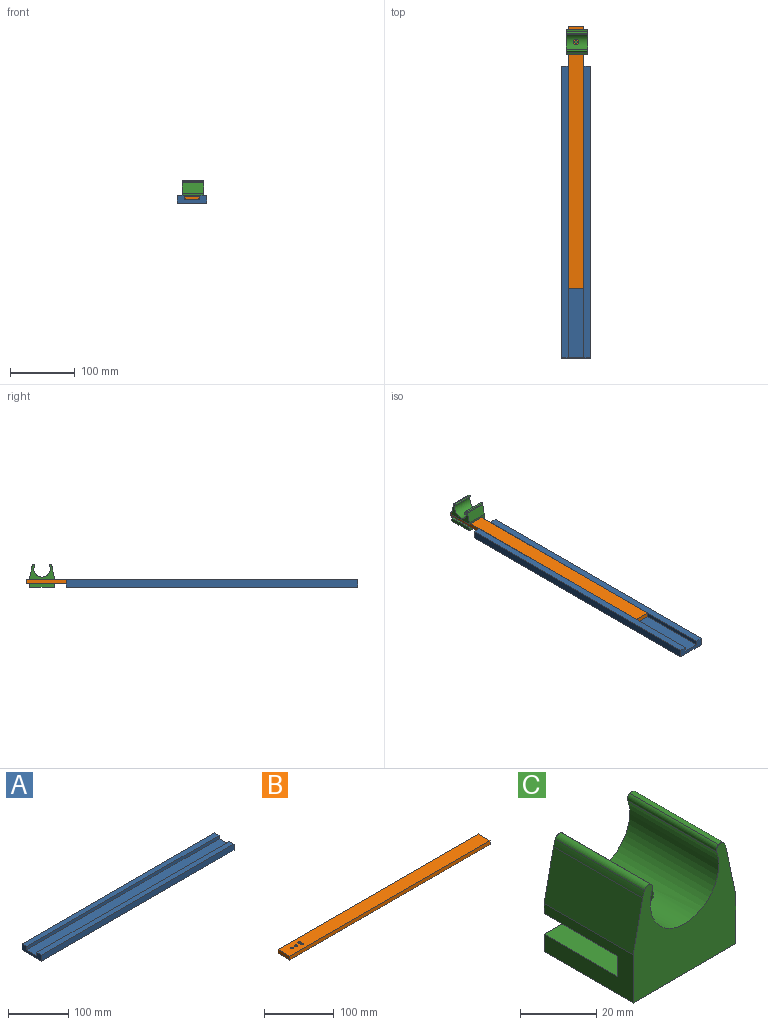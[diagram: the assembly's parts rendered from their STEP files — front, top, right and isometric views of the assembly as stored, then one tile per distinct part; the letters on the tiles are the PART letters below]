
ASSEMBLY  parts=3 mates=2
PART A: 10 faces, bbox 450.9x45.7x12.2 mm
  f0: plane 450.85x6.6mm, normal (0,1,0), area 2977.4mm2, adj f1,f7,f8,f9
  f1: plane 450.85x10.8mm, normal (0,0,1), area 4866.9mm2, adj f0,f2,f8,f9
  f2: plane 450.85x12.19mm, normal (0,-1,0), area 5496.8mm2, adj f1,f3,f8,f9
  f3: plane 450.85x45.72mm, normal (0,0,-1), area 20612.9mm2, adj f2,f4,f8,f9
  f4: plane 450.85x12.19mm, normal (0,1,0), area 5496.8mm2, adj f3,f5,f8,f9
  f5: plane 450.85x10.8mm, normal (0,0,1), area 4866.9mm2, adj f4,f6,f8,f9
  f6: plane 450.85x6.6mm, normal (0,-1,0), area 2977.4mm2, adj f5,f7,f8,f9
  f7: plane 450.85x24.13mm, normal (0,0,1), area 10879mm2, adj f0,f6,f8,f9
  f8: plane 45.72x12.19mm, normal (1,0,0), area 398.1mm2, adj f0,f1,f2,f3,f4,f5,f6,f7
  f9: plane 45.72x12.19mm, normal (-1,0,0), area 398.1mm2, adj f0,f1,f2,f3,f4,f5,f6,f7
PART B: 17 faces, bbox 406.4x24.1x6.6 mm
  f0: plane 406.4x24.13mm, normal (0,0,-1), area 1690.2mm2, adj f7,f9,f10,f11,f12,f13,f14,f15
  f1: cylinder r=2.03mm len=4.06mm, axis (0,0,1), area 25.9mm2, adj f8,f16
  f2: cylinder r=2.16mm len=4.32mm, axis (0,0,1), area 27.6mm2, adj f8,f16
  f3: cylinder r=2.16mm len=4.32mm, axis (0,0,1), area 13.8mm2, adj f4,f6,f8,f16
  f4: plane 4.83x2.03mm, normal (1,0,0), area 9.8mm2, adj f3,f5,f8,f16
  f5: cylinder r=2.16mm len=4.32mm, axis (0,0,1), area 13.8mm2, adj f4,f6,f8,f16
  f6: plane 4.83x2.03mm, normal (-1,0,0), area 9.8mm2, adj f3,f5,f8,f16
  f7: plane 406.4x6.6mm, normal (0,1,0), area 2683.9mm2, adj f0,f8,f10,f11
  f8: plane 406.4x24.13mm, normal (0,0,1), area 9743.3mm2, adj f1,f2,f3,f4,f5,f6,f7,f9
  f9: plane 406.4x6.6mm, normal (0,-1,0), area 2683.9mm2, adj f0,f8,f10,f11
  f10: plane 24.13x6.6mm, normal (1,0,0), area 159.4mm2, adj f0,f7,f8,f9
  f11: plane 24.13x6.6mm, normal (-1,0,0), area 159.4mm2, adj f0,f7,f8,f9
  f12: plane 402.44x4.57mm, normal (0,-1,0), area 1839.9mm2, adj f0,f13,f15,f16
  f13: plane 20.17x4.57mm, normal (-1,0,0), area 92.2mm2, adj f0,f12,f14,f16
  f14: plane 402.44x4.57mm, normal (0,1,0), area 1839.9mm2, adj f0,f13,f15,f16
  f15: plane 20.17x4.57mm, normal (1,0,0), area 92.2mm2, adj f0,f12,f14,f16
  f16: plane 402.44x20.17mm, normal (0,0,-1), area 8053.1mm2, adj f1,f2,f3,f4,f5,f6,f12,f13
PART C: 19 faces, bbox 38.1x33x35.1 mm
  f0: plane 38.1x27.31mm, normal (0,0,1), area 1040.3mm2, adj f1,f5,f6,f7
  f1: plane 38.1x6.6mm, normal (0,1,0), area 251.6mm2, adj f0,f2,f6,f7
  f2: plane 38.1x27.31mm, normal (0,0,-1), area 978.2mm2, adj f1,f3,f6,f7,f17
  f3: plane 38.1x22.91mm, normal (0,1,0), area 374.4mm2, adj f2,f6,f7,f8,f9,f10,f11,f12
  f4: plane 38.1x33.02mm, normal (0,0,-1), area 1258.1mm2, adj f5,f6,f7,f18
  f5: plane 38.1x5.59mm, normal (0,1,0), area 212.9mm2, adj f0,f4,f6,f7
  f6: plane 33.02x15.37mm, normal (1,0,0), area 327.1mm2, adj f0,f1,f2,f3,f4,f5,f10,f18
  f7: plane 33.02x15.37mm, normal (-1,0,0), area 327.1mm2, adj f0,f1,f2,f3,f4,f5,f9,f18
  f8: cylinder r=15.88mm len=33.02mm, axis (0,-1,0), area 74.7mm2, adj f3,f9,f14,f18
  f9: plane 33.02x16.52mm, normal (-0.98,0,0.21), area 557.8mm2, adj f3,f7,f8,f18
  f10: plane 33.02x16.52mm, normal (0.98,0,0.21), area 557.8mm2, adj f3,f6,f11,f18
  f11: cylinder r=15.88mm len=33.02mm, axis (0,-1,0), area 74.7mm2, adj f3,f10,f16,f18
  f12: cylinder r=12.7mm len=33.02mm, axis (0,-1,0), area 1550.3mm2, adj f3,f13,f15,f17,f18
  f13: cylinder r=1.59mm len=33.02mm, axis (0,-1,0), area 76.6mm2, adj f3,f12,f14,f18
  f14: cylinder r=1.59mm len=33.02mm, axis (0,-1,0), area 88.4mm2, adj f3,f8,f13,f18
  f15: cylinder r=1.59mm len=33.02mm, axis (0,-1,0), area 76.6mm2, adj f3,f12,f16,f18
  f16: cylinder r=1.59mm len=33.02mm, axis (0,-1,0), area 88.4mm2, adj f3,f11,f15,f18
  f17: cylinder r=4.45mm len=8.89mm, axis (0,0,-1), area 114mm2, adj f2,f12
  f18: plane 38.1x35.1mm, normal (0,-1,0), area 838.9mm2, adj f4,f6,f7,f8,f9,f10,f11,f12
PLACE A rot(axis=(0,0,-1),90deg) t=(0,0,6.1)mm
PLACE B rot(axis=(0,0,-1),90deg) t=(0,62.43,6.1)mm
PLACE C rot(axis=(0,0,1),90deg) t=(0,18.61,6.1)mm
MATE slider B.f11 <-> A.f9  axis (0,1,0) through (0,62.43,5.59)mm
MATE fastened C.f17 <-> B.f2  axis (0,0,-1) through (0,37.66,12.19)mm
